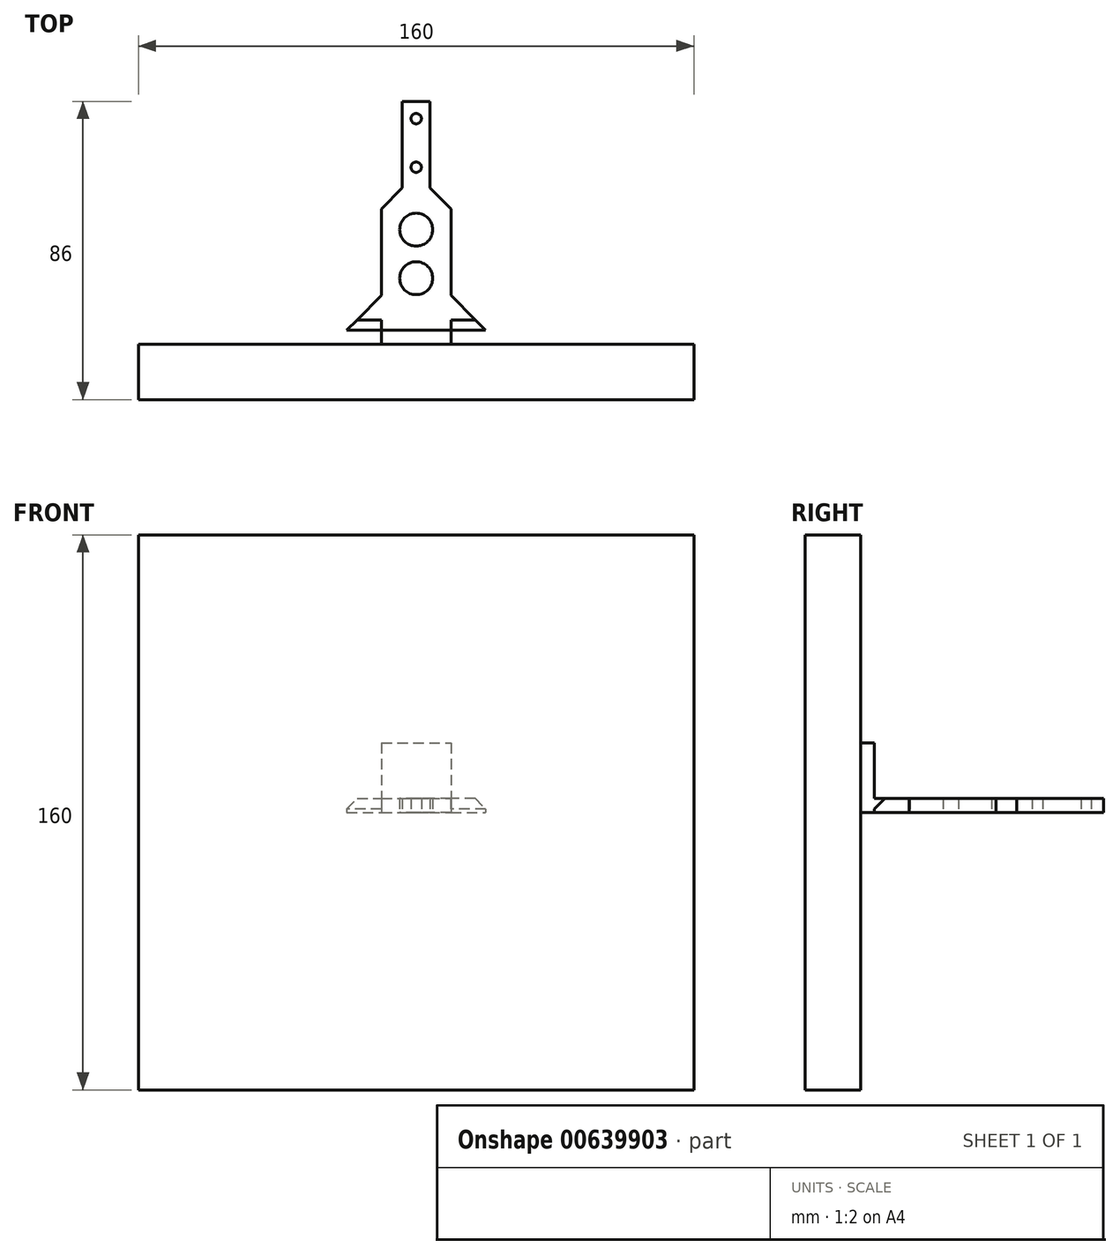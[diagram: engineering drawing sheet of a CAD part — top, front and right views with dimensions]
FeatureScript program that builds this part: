
annotation { "Feature Type Name" : "Feature", "Feature Type Description" : "" }
export const myFeature = defineFeature(function(context is Context, id is Id, definition is map)
    precondition{}
    {
        {
            var Q0;
            Q0=qCreatedBy(makeId("Top.planeOp"),FACE);
            var sketch = newSketch(context, id + "F0", { "sketchPlane" : qUnion([Q0])});
            skLineSegment(sketch, "E0.bottom", {"start": v(-4, 35) * mm, "end": v(4, 35) * mm});
            skLineSegment(sketch, "E0.top", {"start": v(-10, -35) * mm, "end": v(10, -35) * mm});
            skLineSegment(sketch, "E0.left", {"start": v(-10, 4) * mm, "end": v(-10, -35) * mm});
            skLineSegment(sketch, "E0.right", {"start": v(10, 4) * mm, "end": v(10, -35) * mm});
            skLineSegment(sketch, "E1.top", {"start": v(-10, -31) * mm, "end": v(10, -31) * mm});
            skLineSegment(sketch, "E1.left", {"start": v(-10, -35) * mm, "end": v(-10, -31) * mm});
            skLineSegment(sketch, "E1.right", {"start": v(10, -35) * mm, "end": v(10, -31) * mm});
            skCircle(sketch, "E2", {"center": v(0, -16) * mm, "radius": 4.75 * mm});
            skLineSegment(sketch, "E3", {"start": v(-10, -35) * mm, "end": v(-20, -35) * mm});
            skLineSegment(sketch, "E4", {"start": v(-20, -35) * mm, "end": v(-20, -31) * mm});
            skLineSegment(sketch, "E5", {"start": v(-20, -31) * mm, "end": v(-10, -21) * mm});
            skLineSegment(sketch, "E6.MirrorCS", {"start": v(10, -35) * mm, "end": v(20, -35) * mm});
            skLineSegment(sketch, "E7.MirrorCS", {"start": v(20, -35) * mm, "end": v(20, -31) * mm});
            skLineSegment(sketch, "E8.MirrorCS", {"start": v(20, -31) * mm, "end": v(10, -21) * mm});
            skLineSegment(sketch, "E9", {"start": v(-20, -31) * mm, "end": v(-10, -31) * mm});
            skLineSegment(sketch, "E10", {"start": v(10, -31) * mm, "end": v(20, -31) * mm});
            skCircle(sketch, "E11", {"center": v(0, 30) * mm, "radius": 1.5 * mm});
            skCircle(sketch, "E12", {"center": v(0, -2) * mm, "radius": 4.75 * mm});
            skCircle(sketch, "E13", {"center": v(0, 16) * mm, "radius": 1.5 * mm});
            skLineSegment(sketch, "E14", {"start": v(-10, 4) * mm, "end": v(-4, 10) * mm});
            skLineSegment(sketch, "E15", {"start": v(-4, 10) * mm, "end": v(-4, 35) * mm});
            skLineSegment(sketch, "E16.MirrorCS", {"start": v(4, 10) * mm, "end": v(4, 35) * mm});
            skLineSegment(sketch, "E17.MirrorCS", {"start": v(10, 4) * mm, "end": v(4, 10) * mm});
            skSolve(sketch);
        }
        {
            var Q0;
            Q0=makeQuery(id+"F0.imprint","IMPRINT",FACE,{"disambiguationData":[TD([[makeQuery(id+"F0.imprint","IMPRINT",EDGE,{"derivedFrom":sQuery(id+"F0.wireOp",EDGE,"E0.bottom")}),-1.0]])]});
            var Q1;
            {var subQ2=sQuery(id+"F0.wireOp",EDGE,"E5");Q1=makeQuery(id+"F0.imprint","IMPRINT",FACE,{"disambiguationData":[TD([[makeQuery(id+"F0.imprint","IMPRINT",EDGE,{"derivedFrom":subQ2}),-1.0]])]});}
            var Q2;
            {var subQ2=sQuery(id+"F0.wireOp",EDGE,"E8.MirrorCS");Q2=makeQuery(id+"F0.imprint","IMPRINT",FACE,{"disambiguationData":[TD([[makeQuery(id+"F0.imprint","IMPRINT",EDGE,{"derivedFrom":subQ2}),1.0]])]});}
            extrude(context, id + "F1", {"entities" : qUnion([Q0, Q1, Q2]), "depth" : 4 * mm, "offsetDistance" : 25 * mm});
        }
        {
            var Q0;
            Q0=makeQuery(id+"F0.imprint","IMPRINT",FACE,{"disambiguationData":[TD([[makeQuery(id+"F0.imprint","IMPRINT",EDGE,{"derivedFrom":sQuery(id+"F0.wireOp",EDGE,"E0.top")}),1.0]])]});
            var Q1;
            Q1=makeQuery(id+"F0.imprint","IMPRINT",FACE,{"disambiguationData":[TD([[makeQuery(id+"F0.imprint","IMPRINT",EDGE,{"derivedFrom":sQuery(id+"F0.wireOp",EDGE,"E1.left")}),1.0]])]});
            var Q2;
            Q2=makeQuery(id+"F0.imprint","IMPRINT",FACE,{"disambiguationData":[TD([[makeQuery(id+"F0.imprint","IMPRINT",EDGE,{"derivedFrom":sQuery(id+"F0.wireOp",EDGE,"E1.right")}),-1.0]])]});
            extrude(context, id + "F2", {"entities" : qUnion([Q0, Q1, Q2]), "operationType" : NewBodyOperationType.ADD, "depth" : 20 * mm, "offsetDistance" : 25 * mm});
        }
        {
            var Q0;
            Q0=makeQuery(id+"F2.opExtrude","SWEPT_FACE",FACE,{"disambiguationData":[OSD([sQuery(id+"F0.wireOp",EDGE,"E1.top"),sQuery(id+"F0.wireOp",EDGE,"E9"),sQuery(id+"F0.wireOp",EDGE,"E10")])]});
            var sketch = newSketch(context, id + "F3", { "sketchPlane" : qUnion([Q0])});
            skCircle(sketch, "E18", {"center": v(-15, 12) * mm, "radius": 1.6 * mm});
            skPoint(sketch, "E18.centerSnap0", {"position": v(-20, 12) * mm});
            skCircle(sketch, "E19.MirrorC", {"center": v(15, 12) * mm, "radius": 1.6 * mm});
            skSolve(sketch);
        }
        {
            var Q0;
            Q0=makeQuery(id+"F3.imprint","IMPRINT",FACE,{"disambiguationData":[TD([[makeQuery(id+"F3.imprint","IMPRINT",EDGE,{"derivedFrom":sQuery(id+"F3.wireOp",EDGE,"E18")}),1.0]])]});
            var Q1;
            Q1=makeQuery(id+"F3.imprint","IMPRINT",FACE,{"disambiguationData":[TD([[makeQuery(id+"F3.imprint","IMPRINT",EDGE,{"derivedFrom":sQuery(id+"F3.wireOp",EDGE,"E19.MirrorC")}),-1.0]])]});
            var Q2;
            Q2=makeQuery(id+"F2.opExtrude","SWEPT_FACE",FACE,{"disambiguationData":[OSD([sQuery(id+"F0.wireOp",EDGE,"E0.top"),sQuery(id+"F0.wireOp",EDGE,"E3"),sQuery(id+"F0.wireOp",EDGE,"E6.MirrorCS")])]});
            extrude(context, id + "F4", {"entities" : qUnion([Q0, Q1]), "operationType" : NewBodyOperationType.REMOVE, "endBound" : BoundingType.UP_TO_SURFACE, "oppositeDirection" : true, "depth" : 25 * mm, "endBoundEntityFace" : qUnion([Q2]), "offsetDistance" : 25 * mm});
        }
        {
            var Q0;
            Q0=makeQuery(id+"F1.opExtrude","CAP_EDGE",EDGE,{"disambiguationData":[OSD([sQuery(id+"F0.wireOp",EDGE,"E1.top"),sQuery(id+"F0.wireOp",EDGE,"E9"),sQuery(id+"F0.wireOp",EDGE,"E10")])],"isStart":false});
            chamfer(context, id + "F5", {"entities" : qUnion([Q0]), "width" : 3 * mm, "tangentPropagation" : true});
        }
        {
            var Q0;
            Q0=makeQuery(id+"F2.opExtrude","SWEPT_FACE",FACE,{"disambiguationData":[OSD([sQuery(id+"F0.wireOp",EDGE,"E0.top"),sQuery(id+"F0.wireOp",EDGE,"E3"),sQuery(id+"F0.wireOp",EDGE,"E6.MirrorCS")])]});
            var sketch = newSketch(context, id + "F6", { "sketchPlane" : qUnion([Q0])});
            skLineSegment(sketch, "E20.bottom", {"start": v(-80, 80) * mm, "end": v(80, 80) * mm});
            skLineSegment(sketch, "E20.top", {"start": v(-80, -80) * mm, "end": v(80, -80) * mm});
            skLineSegment(sketch, "E20.left", {"start": v(-80, 80) * mm, "end": v(-80, -80) * mm});
            skLineSegment(sketch, "E20.right", {"start": v(80, 80) * mm, "end": v(80, -80) * mm});
            skPoint(sketch, "E20.middle", {"position": v(0, 0) * mm});
            skSolve(sketch);
        }
        {
            var Q0;
            Q0=makeQuery(id+"F6.imprint","IMPRINT",FACE,{"disambiguationData":[TD([[makeQuery(id+"F6.imprint","IMPRINT",EDGE,{"derivedFrom":makeQuery(id+"F4.boolean.opBoolean","COPY",EDGE,{"derivedFrom":makeQuery(id+"F4.opExtrude","TWEAK_EDGE",EDGE,{"derivedFrom":[makeQuery(id+"F2.opExtrude","SWEPT_FACE",FACE,{"disambiguationData":[OSD([sQuery(id+"F0.wireOp",EDGE,"E0.top"),sQuery(id+"F0.wireOp",EDGE,"E3"),sQuery(id+"F0.wireOp",EDGE,"E6.MirrorCS")])]}),makeQuery(id+"F3.imprint","IMPRINT",EDGE,{"derivedFrom":sQuery(id+"F3.wireOp",EDGE,"E18")})]})})}),1.0]])]});
            var Q1;
            Q1=makeQuery(id+"F6.imprint","IMPRINT",FACE,{"disambiguationData":[TD([[makeQuery(id+"F6.imprint","IMPRINT",EDGE,{"derivedFrom":makeQuery(id+"F4.boolean.opBoolean","COPY",EDGE,{"derivedFrom":makeQuery(id+"F4.opExtrude","TWEAK_EDGE",EDGE,{"derivedFrom":[makeQuery(id+"F2.opExtrude","SWEPT_FACE",FACE,{"disambiguationData":[OSD([sQuery(id+"F0.wireOp",EDGE,"E0.top"),sQuery(id+"F0.wireOp",EDGE,"E3"),sQuery(id+"F0.wireOp",EDGE,"E6.MirrorCS")])]}),makeQuery(id+"F3.imprint","IMPRINT",EDGE,{"derivedFrom":sQuery(id+"F3.wireOp",EDGE,"E19.MirrorC")})]})})}),-1.0]])]});
            var Q2;
            {var subQ1=sQuery(id+"F0.wireOp",EDGE,"E3");Q2=makeQuery(id+"F6.imprint","IMPRINT",FACE,{"disambiguationData":[TD([[makeQuery(id+"F6.imprint","IMPRINT",EDGE,{"derivedFrom":makeQuery(id+"F2.opExtrude","SWEPT_EDGE",EDGE,{"disambiguationData":[OSD([subQ1,sQuery(id+"F0.wireOp",EDGE,"E4")])]})}),1.0]])]});}
            var Q3;
            Q3=makeQuery(id+"F6.imprint","IMPRINT",FACE,{"disambiguationData":[TD([[makeQuery(id+"F6.imprint","IMPRINT",EDGE,{"derivedFrom":sQuery(id+"F6.wireOp",EDGE,"E20.bottom")}),-1.0]])]});
            extrude(context, id + "F7", {"entities" : qUnion([Q0, Q1, Q2, Q3]), "depth" : 16 * mm, "offsetDistance" : 25 * mm});
        }
    });
